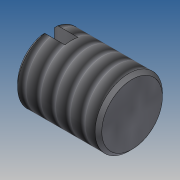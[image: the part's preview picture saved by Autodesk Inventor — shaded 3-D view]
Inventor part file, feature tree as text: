
AUTODESK INVENTOR PART (.ipt)
format: ipt  version: 2018.3 (Build 223284000, 284)  size: 129,024 bytes
history: native  units: in
note: dims shown in document units (in); Inventor stores cm internally (conversion verified against a paired STEP export)
features: thread x1, other x1
ambient origin geometry x8: Origin, YZ Plane, XZ Plane, XY Plane, X Axis, Y Axis, Z Axis, Center Point
bodies: Solid1 (feature_tree)
feature tree (2):
  thread  "Thread1"  [1 undecoded]
  parser-record x1  (decoder bookkeeping rows leaked as tree rows — omitted from the tree; the rows remain in map.json)
note: 1 required parameter value undecoded (feature->parameter linkage not recoverable at this tier; creation-order binding heuristic only, values carry confidence <= 0.55)
